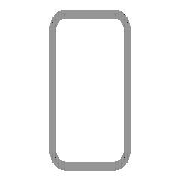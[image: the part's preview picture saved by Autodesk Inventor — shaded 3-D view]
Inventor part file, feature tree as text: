
AUTODESK INVENTOR PART (.ipt)
format: ipt  version: 2025 (Build 290162010, 162A)  size: 134,144 bytes
history: native  units: mm (DEFAULTED — no unit token found)
features: other x4, sketch x1, plane x1
ambient origin geometry x8: Origin, YZ Plane, XZ Plane, XY Plane, X Axis, Y Axis, Z Axis, Center Point
bodies: Solid1 (feature_tree), Body (feature_tree)
feature tree (6):
  parser-record x1  (decoder bookkeeping rows leaked as tree rows — omitted from the tree; the rows remain in map.json)
  other  "Driven Length"
  other  "Start plane"
  other  "End plane"
  sketch  "Sketch3"  dims[d3=1600.0mm d4=0.0mm d7=6.0mm d9=40.0mm d11=60.0mm d12=3.0mm d13=-0.0mm d14=1600.0mm d15=20.0mm d16=30.0mm d17=90.0deg d18=1600.0mm]
  plane  "Work Plane3"
